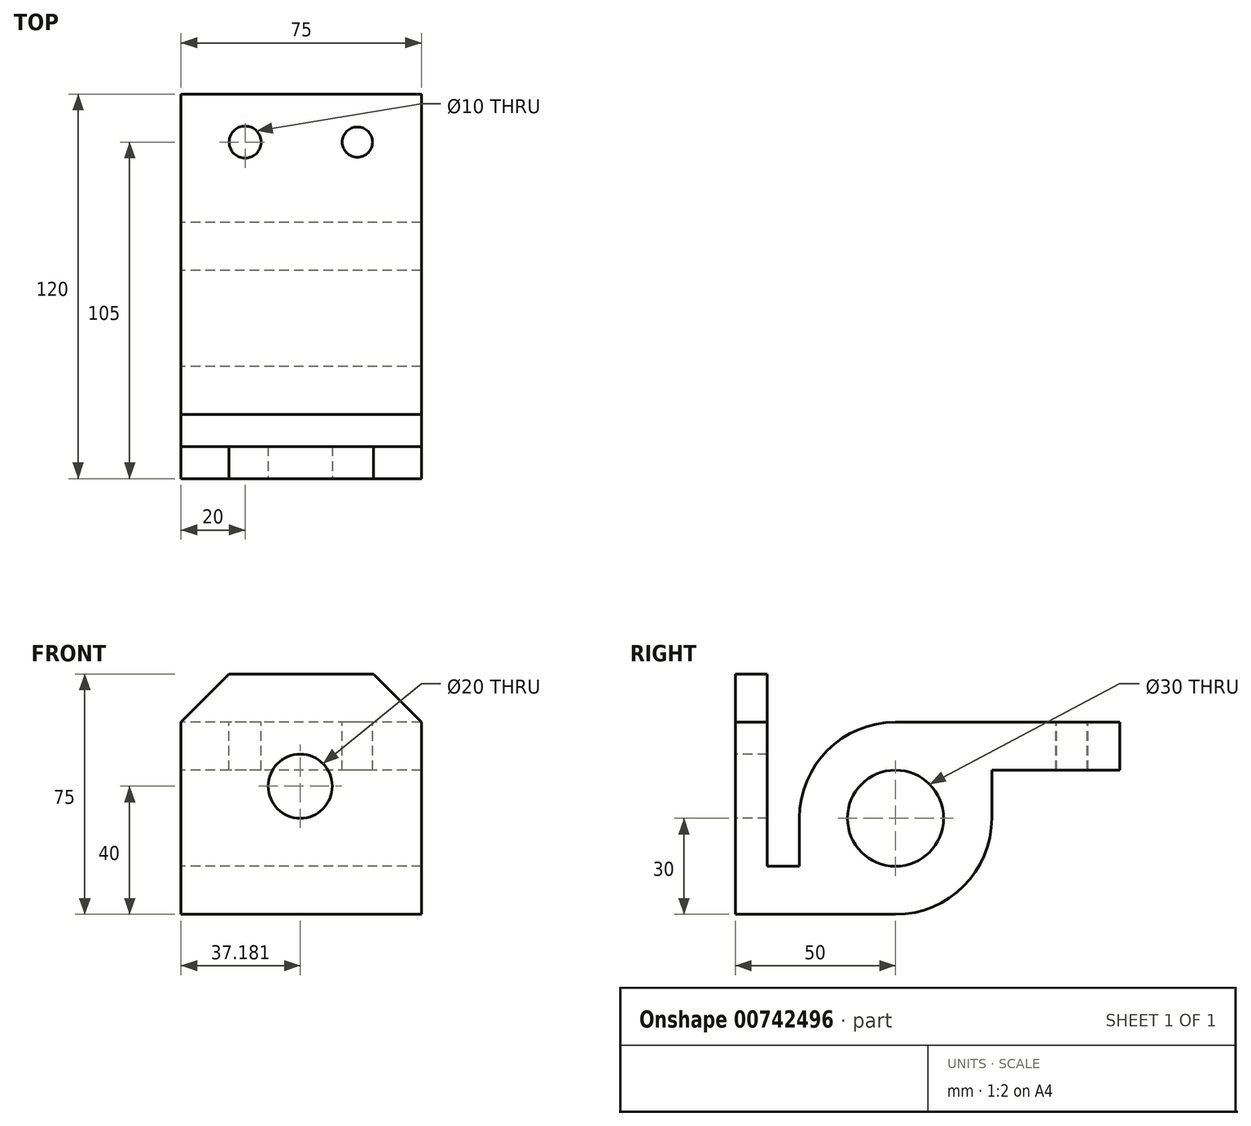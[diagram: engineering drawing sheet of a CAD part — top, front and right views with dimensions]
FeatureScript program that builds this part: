
annotation { "Feature Type Name" : "Feature", "Feature Type Description" : "" }
export const myFeature = defineFeature(function(context is Context, id is Id, definition is map)
    precondition{}
    {
        {
            var Q0;
            Q0=qCreatedBy(makeId("Right.planeOp"),FACE);
            var sketch = newSketch(context, id + "F0", { "sketchPlane" : qUnion([Q0])});
            skCircle(sketch, "E0", {"center": v(0, 0) * mm, "radius": 15 * mm});
            skArc(sketch, "E1", {"start": v(0, -30) * mm, "mid": v(21.21, -21.21) * mm, "end": v(30, 0) * mm});
            skLineSegment(sketch, "E2", {"start": v(0, 30) * mm, "end": v(70, 30) * mm});
            skPoint(sketch, "E3", {"position": v(0, -30) * mm});
            skLineSegment(sketch, "E4", {"start": v(0, -30) * mm, "end": v(-50, -30) * mm});
            skLineSegment(sketch, "E5", {"start": v(-50, 0) * mm, "end": v(-50, -30) * mm});
            skLineSegment(sketch, "E6", {"start": v(-50, -30) * mm, "end": v(-50, 45) * mm});
            skLineSegment(sketch, "E7", {"start": v(-50, 45) * mm, "end": v(-40, 45) * mm});
            skLineSegment(sketch, "E8", {"start": v(-40, 45) * mm, "end": v(-40, -15) * mm});
            skPoint(sketch, "E9", {"position": v(0, -15) * mm});
            skPoint(sketch, "E10", {"position": v(-30, 0) * mm});
            skLineSegment(sketch, "E11", {"start": v(-30, 0) * mm, "end": v(-30, -15) * mm});
            skLineSegment(sketch, "E12", {"start": v(70, 30) * mm, "end": v(70, 15) * mm});
            skLineSegment(sketch, "E13", {"start": v(70, 15) * mm, "end": v(30, 15) * mm});
            skPoint(sketch, "E14", {"position": v(30, 0) * mm});
            skLineSegment(sketch, "E15", {"start": v(30, 0) * mm, "end": v(30, 15) * mm});
            skArc(sketch, "E16.trimOffspring", {"start": v(0, 30) * mm, "mid": v(-21.21, 21.21) * mm, "end": v(-30, 0) * mm});
            skPoint(sketch, "E17", {"position": v(-50, -15) * mm});
            skLineSegment(sketch, "E18", {"start": v(-40, -15) * mm, "end": v(-30, -15) * mm});
            skSolve(sketch);
        }
        {
            var Q0;
            Q0=makeQuery(id+"F0.imprint","IMPRINT",FACE,{"disambiguationData":[TD([[makeQuery(id+"F0.imprint","IMPRINT",EDGE,{"derivedFrom":sQuery(id+"F0.wireOp",EDGE,"E0")}),-1.0]])]});
            extrude(context, id + "F1", {"entities" : qUnion([Q0]), "depth" : 75 * mm, "offsetDistance" : 25 * mm});
        }
        {
            var Q0;
            Q0=makeQuery(id+"F1.opExtrude","CAP_EDGE",EDGE,{"disambiguationData":[OSD([sQuery(id+"F0.wireOp",EDGE,"E7")])],"isStart":false});
            chamfer(context, id + "F2", {"entities" : qUnion([Q0]), "width" : 15 * mm, "tangentPropagation" : true});
        }
        {
            var Q0;
            Q0=makeQuery(id+"F1.opExtrude","CAP_EDGE",EDGE,{"disambiguationData":[OSD([sQuery(id+"F0.wireOp",EDGE,"E7")])],"isStart":true});
            chamfer(context, id + "F3", {"entities" : qUnion([Q0]), "width" : 15 * mm, "tangentPropagation" : true});
        }
        {
            var Q0;
            Q0=makeQuery(id+"F1.opExtrude","SWEPT_FACE",FACE,{"disambiguationData":[OSD([sQuery(id+"F0.wireOp",EDGE,"E6")])]});
            var sketch = newSketch(context, id + "F4", { "sketchPlane" : qUnion([Q0])});
            skCircle(sketch, "E19", {"center": v(37.18, 10) * mm, "radius": 10 * mm});
            skSolve(sketch);
        }
        {
            var Q0;
            Q0=makeQuery(id+"F4.imprint","IMPRINT",FACE,{"disambiguationData":[TD([[makeQuery(id+"F4.imprint","IMPRINT",EDGE,{"derivedFrom":sQuery(id+"F4.wireOp",EDGE,"E19")}),1.0]])]});
            extrude(context, id + "F5", {"entities" : qUnion([Q0]), "operationType" : NewBodyOperationType.REMOVE, "oppositeDirection" : true, "depth" : 15 * mm, "offsetDistance" : 25 * mm});
        }
        {
            var Q0;
            Q0=makeQuery(id+"F1.opExtrude","SWEPT_FACE",FACE,{"disambiguationData":[OSD([sQuery(id+"F0.wireOp",EDGE,"E2")])]});
            var sketch = newSketch(context, id + "F6", { "sketchPlane" : qUnion([Q0])});
            skCircle(sketch, "E20", {"center": v(20, 55) * mm, "radius": 5 * mm});
            skCircle(sketch, "E21", {"center": v(55, 55) * mm, "radius": 4.72 * mm});
            skSolve(sketch);
        }
        {
            var Q0;
            Q0=makeQuery(id+"F6.imprint","IMPRINT",FACE,{"disambiguationData":[TD([[makeQuery(id+"F6.imprint","IMPRINT",EDGE,{"derivedFrom":sQuery(id+"F6.wireOp",EDGE,"E21")}),1.0]])]});
            var Q1;
            Q1=makeQuery(id+"F6.imprint","IMPRINT",FACE,{"disambiguationData":[TD([[makeQuery(id+"F6.imprint","IMPRINT",EDGE,{"derivedFrom":sQuery(id+"F6.wireOp",EDGE,"E20")}),1.0]])]});
            extrude(context, id + "F7", {"entities" : qUnion([Q0, Q1]), "operationType" : NewBodyOperationType.REMOVE, "oppositeDirection" : true, "depth" : 15 * mm, "offsetDistance" : 25 * mm});
        }
    });
